# Revit family: Bowl_Himacs_CB540R
name_source: partatom
category: Plumbing Fixtures
revit_build: Autodesk Revit Architecture 2012 (Build: 20110916_2132(x64)
units: mm (PartAtom-declared; Revit-internal decimal feet)

## types (1)
- Bowl_Himacs_CB540R
    BIMobject category = Sanitary
    Depth = 370 mm  [stored 1.21391 ft]
    Description = HI-MACS® Bowls offer superb ease of cleaning and a warm and pleasant feel, making them the ideal solution for creating the bathroom of your dreams. They are manufactured using a casting process and ideally suited for both flush mounting and installation into a bathroom vanity top
    Design country = Italy
    Edition number = 1
    Height = 130 mm  [stored 0.426509 ft]
    IFC Classification = Furnishing Element
    Installation instructions = http://himacs.eu
    Manufacturer URL = http://himacs.eu
    Manufacturer country = Italy
    Manufacturer name = HI-MACS
    Material Main = Natural Acrylic Stone_Himacs_CB330C_ S28 Alpine White
    Material Secondary = Steel_Himacs_CS824D_Polished
    NBS Reference Code = 35-65-70-94
    NBS Reference Description = Wash Basin Systems
    Nominal height = 130.0
    Nominal width = 580.0
    Product SKU = CB540R
    Product data url = http://himacs.bimobject.com
    Product family = Sinks, Baby Baths & Bowls
    Product group = Bowls
    QR code = http://himacs.bimobject.com
    Technical description = http://himacs.eu
    UNSPSC Code = 301815
    Uniclass 1.4 Code = L7212
    Uniclass 1.4 Description = Washbasins
    Uniclass 2.0 Code = SS-35-65-70-94
    Uniclass 2.0 Description = Wash Basin Systems
    Weight Net (Kg) = 9,5
    Width = 580 mm  [stored 1.90289 ft]

note: [stored X ft] marks values corroborated as IEEE doubles in the binary element streams (Revit-internal decimal feet)

## geometry (parser evidence)
native form markers: Blend x2, Sweep x5
no freeform markers — native parametric forms only
